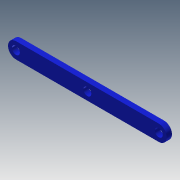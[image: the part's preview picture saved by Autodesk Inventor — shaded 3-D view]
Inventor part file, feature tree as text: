
AUTODESK INVENTOR PART (.ipt)
format: ipt  version: 2013 (Build 170138000, 138)  size: 91,136 bytes
history: native  units: mm
features: extrude x2, sketch x2
ambient origin geometry x8: Origin, YZ Plane, XZ Plane, XY Plane, X Axis, Y Axis, Z Axis, Center Point
bodies: Solid1 (feature_tree)
feature tree (4):
  extrude  "Extrusion1"  Depth=6.0mm
  extrude  "Extrusion2"  Depth=6.0mm
  sketch  "Sketch1"  dims[d0=54.0mm d1=6.0mm]
  sketch  "Sketch2"  dims[d2=6.0mm d3=6.0mm d4=2.0mm d5=0.0mm d6=3.0mm d7=3.0mm d8=3.0mm d9=2.0mm d10=0.0mm]
